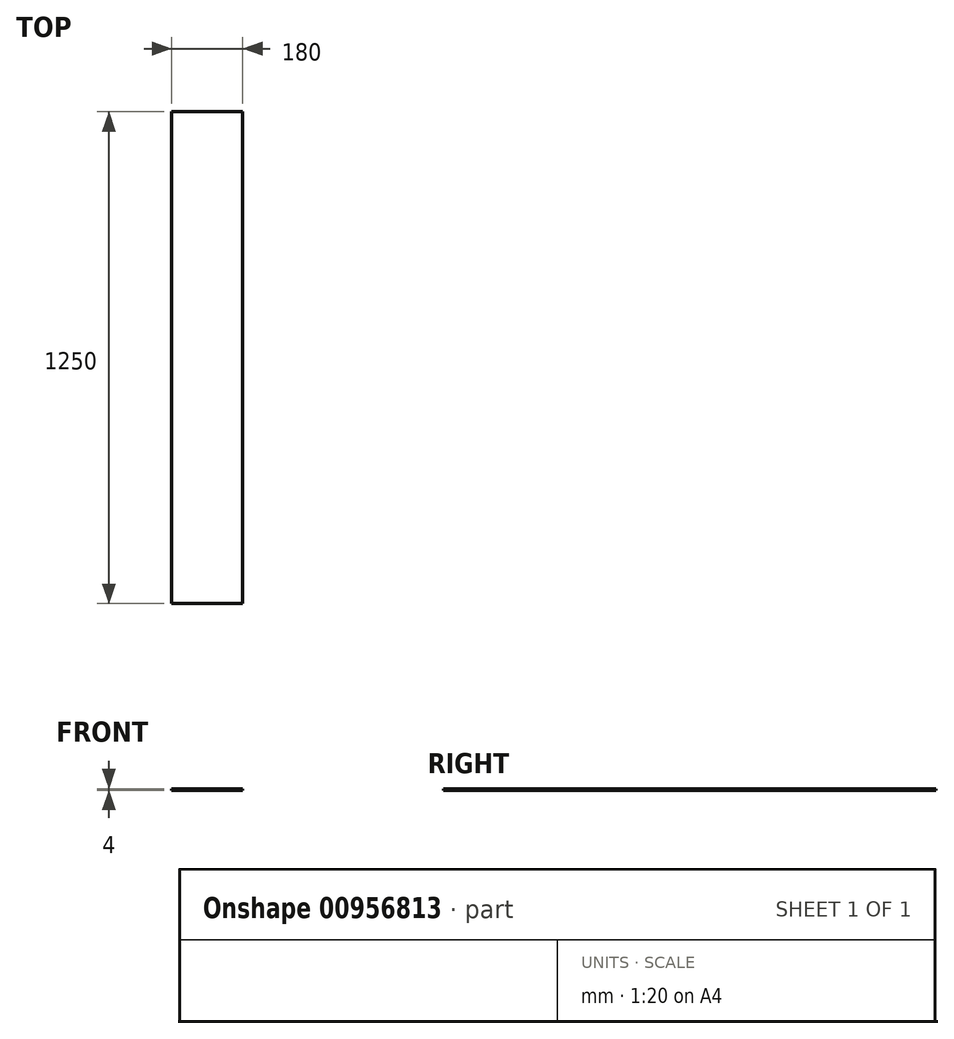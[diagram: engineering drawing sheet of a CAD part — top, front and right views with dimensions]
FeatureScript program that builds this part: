
annotation { "Feature Type Name" : "Feature", "Feature Type Description" : "" }
export const myFeature = defineFeature(function(context is Context, id is Id, definition is map)
    precondition{}
    {
        {
            var Q0;
            Q0=qCreatedBy(makeId("Top.planeOp"),FACE);
            var sketch = newSketch(context, id + "F0", { "sketchPlane" : qUnion([Q0])});
            skLineSegment(sketch, "E0.bottom", {"start": v(90, 625) * mm, "end": v(-90, 625) * mm});
            skLineSegment(sketch, "E0.top", {"start": v(90, -625) * mm, "end": v(-90, -625) * mm});
            skLineSegment(sketch, "E0.left", {"start": v(90, 625) * mm, "end": v(90, -625) * mm});
            skLineSegment(sketch, "E0.right", {"start": v(-90, 625) * mm, "end": v(-90, -625) * mm});
            skPoint(sketch, "E0.middle", {"position": v(0, 0) * mm});
            skSolve(sketch);
        }
        {
            var Q0;
            Q0 = qSketchRegion(id + "F0", true);
            extrude(context, id + "F1", {"entities" : qUnion([Q0]), "depth" : 4 * mm, "offsetDistance" : 25 * mm});
        }
    });
